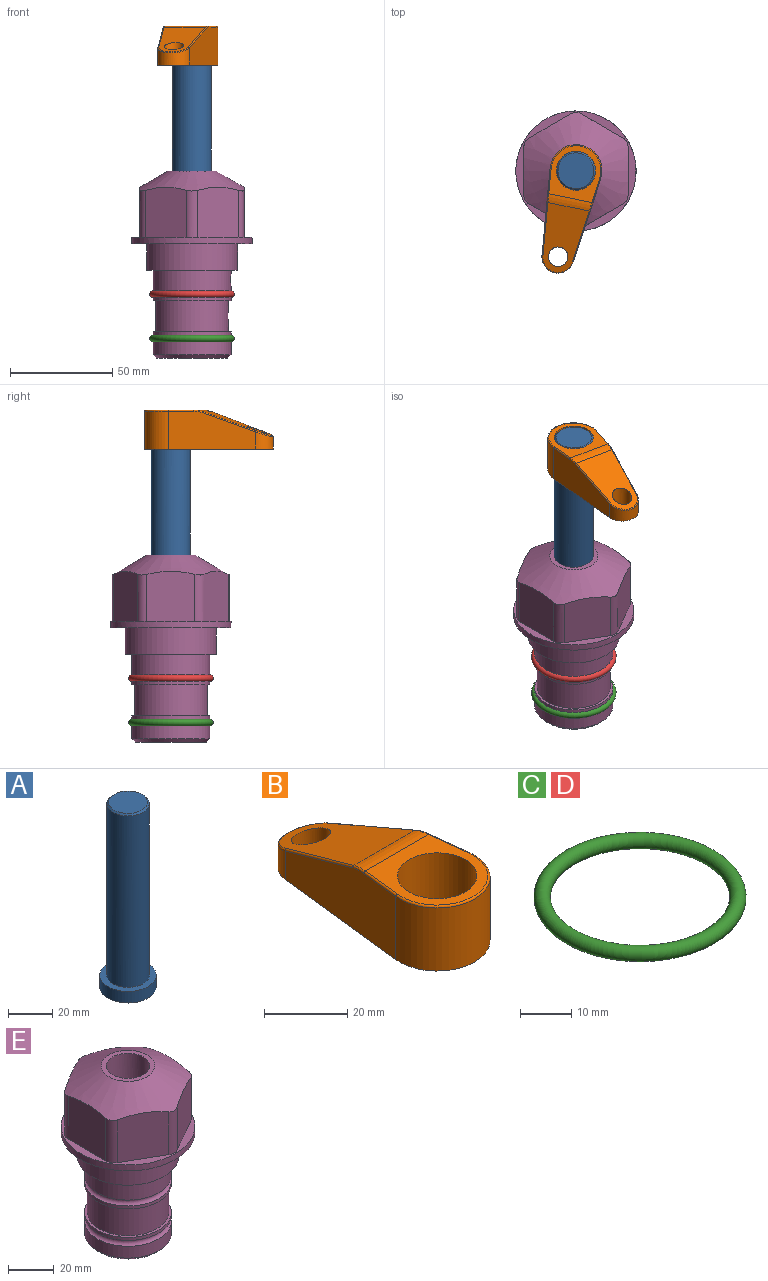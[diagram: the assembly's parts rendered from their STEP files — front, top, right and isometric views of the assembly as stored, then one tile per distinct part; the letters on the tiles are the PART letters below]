
ASSEMBLY  parts=5 mates=3
PART A: 6 faces, bbox 25.4x25.4x101.6 mm
  f0: plane 17.46x17.46mm, normal (0,0,1), area 239.5mm2, adj f5
  f1: plane 25.4x25.4mm, normal (0,0,-1), area 506.7mm2, adj f2
  f2: cylinder r=12.7mm len=25.4mm, axis (0,0,1), area 506.7mm2, adj f1,f3
  f3: plane 25.4x25.4mm, normal (0,0,1), area 221.7mm2, adj f2,f4
  f4: cylinder r=9.53mm len=94.46mm, axis (0,0,1), area 5653mm2, adj f3,f5
  f5: cone r=8.73mm half-angle=45deg, axis (0,0,-1), area 64.4mm2, adj f0,f4
PART B: 44 faces, bbox 27.5x64.5x19.1 mm
  f0: plane 2.3x0.95mm, normal (0,0,-1), area 1mm2, adj f25,f30,f34
  f1: plane 63.5x25.4mm, normal (0,0,-1), area 561.7mm2, adj f2,f3,f4,f5,f6,f7,f19,f20
  f2: cylinder r=12.7mm len=25.4mm, axis (0,0,-1), area 792.2mm2, adj f1,f3,f5,f13
  f3: plane 42.33x18.54mm, normal (0.99,0.11,0), area 647mm2, adj f1,f2,f4,f11,f12,f14
  f4: cylinder r=7.94mm len=15.78mm, axis (0,0,-1), area 158.6mm2, adj f1,f3,f5,f16
  f5: plane 42.33x18.54mm, normal (-0.99,0.11,0), area 647mm2, adj f1,f2,f4,f15,f17,f18
  f6: cylinder r=9.53mm len=19.05mm, axis (0,0,-1), area 1140.1mm2, adj f1,f8
  f7: cylinder r=4.76mm len=10.98mm, axis (0,0,-1), area 276.1mm2, adj f1,f9
  f8: plane 25.83x24.38mm, normal (0,0,1), area 262.2mm2, adj f6,f10,f11,f13,f15
  f9: plane 32.49x20.55mm, normal (0,0.34,0.94), area 489.9mm2, adj f7,f10,f14,f16,f18
  f10: cylinder r=12.7mm len=21.49mm, axis (-1,0,0), area 93.2mm2, adj f8,f9,f12,f17
  f11: cylinder r=0.51mm len=12.34mm, axis (0.11,-0.99,0), area 9.9mm2, adj f3,f8,f12,f13
  f12: bspline ~7.62x1.64mm, area 3.5mm2, adj f3,f10,f11,f14
  f13: torus R=12.19mm, axis (0,0,1), area 33.6mm2, adj f2,f8,f11,f15
  f14: cylinder r=0.51mm len=26.01mm, axis (0.1,-0.93,0.34), area 21.6mm2, adj f3,f9,f12,f16
  f15: cylinder r=0.51mm len=12.34mm, axis (0.11,0.99,0), area 9.9mm2, adj f5,f8,f13,f17
  f16: bspline ~15.78x7.05mm, area 15.7mm2, adj f4,f9,f14,f18
  f17: bspline ~7.62x1.64mm, area 3.5mm2, adj f5,f10,f15,f18
  f18: cylinder r=0.51mm len=26.01mm, axis (0.1,0.93,-0.34), area 21.6mm2, adj f5,f9,f16,f17
  f19: plane 21.6x14.29mm, normal (-0.99,-0.11,0), area 242.6mm2, adj f1,f26,f28,f34,f36,f38
  f20: plane 21.6x14.29mm, normal (0.99,-0.11,0), area 242.6mm2, adj f1,f27,f29,f37,f39,f41
  f21: cylinder r=12.7mm len=14.29mm, axis (0,0,-1), area 173.2mm2, adj f1,f26,f27,f30,f31,f33
  f22: cylinder r=7.94mm len=7.63mm, axis (0,0,-1), area 53.8mm2, adj f1,f28,f29,f42
  f23: plane 2.3x0.95mm, normal (0,0,-1), area 1mm2, adj f25,f33,f37
  f24: plane 17.94x12.32mm, normal (0,-0.34,-0.94), area 191.2mm2, adj f25,f38,f41,f42
  f25: cylinder r=9.53mm len=12.93mm, axis (-1,0,0), area 37.5mm2, adj f0,f23,f24,f31,f36,f39
  f26: cylinder r=1.59mm len=14.29mm, axis (0,0,-1), area 49mm2, adj f1,f19,f21,f32
  f27: cylinder r=1.59mm len=14.29mm, axis (0,0,-1), area 49mm2, adj f1,f20,f21,f35
  f28: cylinder r=1.59mm len=7.28mm, axis (0,0,-1), area 22.1mm2, adj f1,f19,f22,f40
  f29: cylinder r=1.59mm len=7.28mm, axis (0,0,-1), area 22.1mm2, adj f1,f20,f22,f43
  f30: torus R=14.29mm, axis (0,0,1), area 5.8mm2, adj f0,f21,f31,f32
  f31: bspline ~11.06x2.73mm, area 20.8mm2, adj f21,f25,f30,f33
  f32: sphere r=1.59mm, area 5.4mm2, adj f26,f30,f34
  f33: torus R=14.29mm, axis (0,0,1), area 5.8mm2, adj f21,f23,f31,f35
  f34: cylinder r=1.59mm len=1.68mm, axis (-0.11,0.99,0), area 2.4mm2, adj f0,f19,f32,f36
  f35: sphere r=1.59mm, area 5.4mm2, adj f27,f33,f37
  f36: bspline ~5.82x2.33mm, area 7.7mm2, adj f19,f25,f34,f38
  f37: cylinder r=1.59mm len=1.68mm, axis (0.11,0.99,0), area 2.4mm2, adj f20,f23,f35,f39
  f38: cylinder r=1.59mm len=18.33mm, axis (0.1,-0.93,0.34), area 46.7mm2, adj f19,f24,f36,f40
  f39: bspline ~5.82x2.33mm, area 7.7mm2, adj f20,f25,f37,f41
  f40: sphere r=1.59mm, area 3.6mm2, adj f28,f38,f42
  f41: cylinder r=1.59mm len=18.33mm, axis (0.1,0.93,-0.34), area 46.7mm2, adj f20,f24,f39,f43
  f42: bspline ~8.31x1.84mm, area 15.3mm2, adj f22,f24,f40,f43
  f43: sphere r=1.59mm, area 3.6mm2, adj f29,f41,f42
PART C: 1 faces, bbox 44.7x44.7x3.2 mm
  f0: torus R=19.05mm, axis (0,0,1), area 1193.9mm2
PART D: same geometry as C
PART E: 36 faces, bbox 58.7x58.7x91.2 mm
  f0: cylinder r=17.78mm len=35.56mm, axis (0,0,1), area 1670.8mm2, adj f23,f24,f31
  f1: cylinder r=19.05mm len=38.1mm, axis (0,0,1), area 1191.9mm2, adj f26,f27,f30
  f2: plane 58.66x58.66mm, normal (0,0,-1), area 1150.6mm2, adj f3,f28
  f3: cylinder r=29.33mm len=58.66mm, axis (0,0,-1), area 585.1mm2, adj f2,f4
  f4: plane 58.66x58.66mm, normal (0,0,1), area 475.9mm2, adj f3,f5,f6,f7,f8,f9,f10,f11
  f5: plane 24.5x20.32mm, normal (-0.5,0.87,0), area 562.8mm2, adj f4,f15,f16,f17
  f6: plane 24.5x20.32mm, normal (0.5,0.87,0), area 562.8mm2, adj f4,f14,f15,f17
  f7: plane 24.5x23.48mm, normal (1,0,0), area 562.8mm2, adj f4,f13,f14,f17
  f8: plane 24.5x20.32mm, normal (0.5,-0.87,0), area 562.8mm2, adj f4,f12,f13,f17
  f9: plane 24.5x20.32mm, normal (-0.5,-0.87,0), area 562.8mm2, adj f4,f11,f12,f17
  f10: plane 24.5x23.48mm, normal (-1,0,0), area 562.8mm2, adj f4,f11,f16,f17
  f11: cylinder r=5.08mm len=23.01mm, axis (0,0,-1), area 121.2mm2, adj f4,f9,f10,f17
  f12: cylinder r=5.08mm len=23.01mm, axis (0,0,-1), area 121.2mm2, adj f4,f8,f9,f17
  f13: cylinder r=5.08mm len=23.01mm, axis (0,0,-1), area 121.2mm2, adj f4,f7,f8,f17
  f14: cylinder r=5.08mm len=23.01mm, axis (0,0,-1), area 121.2mm2, adj f4,f6,f7,f17
  f15: cylinder r=5.08mm len=23.01mm, axis (0,0,-1), area 121.2mm2, adj f4,f5,f6,f17
  f16: cylinder r=5.08mm len=23.01mm, axis (0,0,-1), area 121.2mm2, adj f4,f5,f10,f17
  f17: cone r=11.73mm half-angle=60deg, axis (0,0,-1), area 2071.8mm2, adj f5,f6,f7,f8,f9,f10,f11,f12
  f18: plane 23.46x23.46mm, normal (0,0,1), area 147.4mm2, adj f17,f35
  f19: plane 34.93x34.93mm, normal (0,0,-1), area 958mm2, adj f29
  f20: cylinder r=19.05mm len=38.1mm, axis (0,0,1), area 760.1mm2, adj f21,f29
  f21: torus R=19.05mm, axis (0,0,1), area 565.3mm2, adj f20,f22
  f22: cylinder r=19.05mm len=38.1mm, axis (0,0,1), area 190mm2, adj f21,f23
  f23: plane 38.1x38.1mm, normal (0,0,1), area 146.9mm2, adj f0,f22
  f24: plane 38.1x38.1mm, normal (0,0,-1), area 146.9mm2, adj f0,f25
  f25: cylinder r=19.05mm len=38.1mm, axis (0,0,1), area 190mm2, adj f24,f26
  f26: torus R=19.05mm, axis (0,0,1), area 565.3mm2, adj f1,f25
  f27: plane 44.45x44.45mm, normal (0,0,-1), area 411.7mm2, adj f1,f28
  f28: cylinder r=22.23mm len=44.45mm, axis (0,0,1), area 1773.5mm2, adj f2,f27
  f29: cone r=19.05mm half-angle=45deg, axis (0,0,1), area 257.5mm2, adj f19,f20
  f30: cylinder r=3.17mm len=6.75mm, axis (-1,0,0), area 128mm2, adj f1,f33
  f31: cylinder r=3.17mm len=6.35mm, axis (-1,0,0), area 102.5mm2, adj f0,f33
  f32: plane 25.4x25.4mm, normal (0,0,1), area 506.7mm2, adj f33
  f33: cylinder r=12.7mm len=66.42mm, axis (0,0,-1), area 5236.2mm2, adj f30,f31,f32,f34
  f34: cone r=9.53mm half-angle=30deg, axis (0,0,-1), area 443.4mm2, adj f33,f35
  f35: cylinder r=9.53mm len=19.05mm, axis (0,0,-1), area 849mm2, adj f18,f34
PLACE A rot(axis=(0,0,-1),101.7deg) t=(0,0,32.7)mm
PLACE B rot(axis=(0,0,1),168.3deg) t=(0,0,87.31)mm
PLACE C t=(0,0,-21.59)mm
PLACE D at identity
PLACE E at identity fixed
MATE fastened C.f0 <-> E.f0  axis (0,0,1) through (0,0,-46.1)mm
MATE cylindrical A.f2 <-> E.f0  axis (0,0,1) through (0,0,58.34)mm
MATE fastened B.f2 <-> A.f2  axis (0,0,1) through (0,0,106.36)mm
